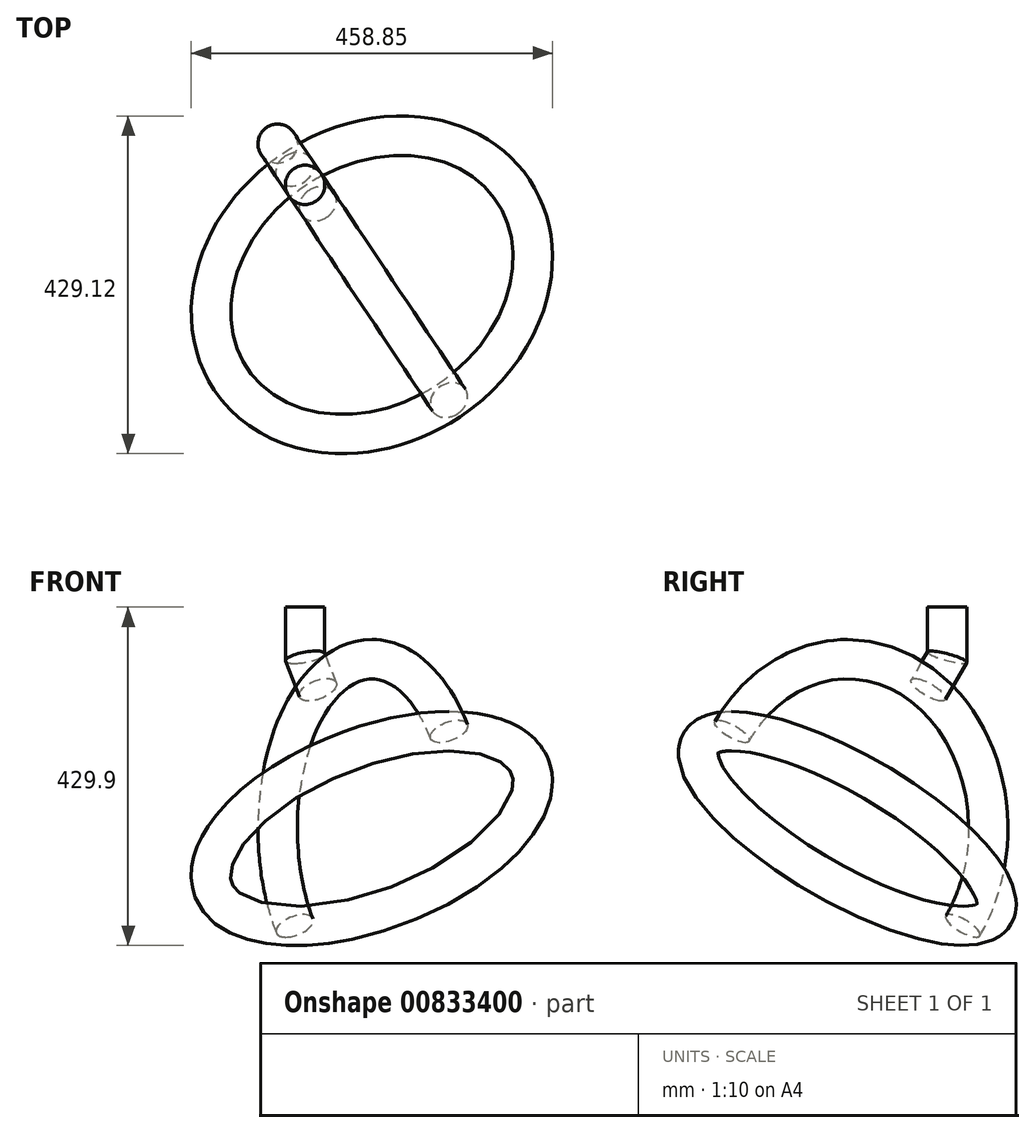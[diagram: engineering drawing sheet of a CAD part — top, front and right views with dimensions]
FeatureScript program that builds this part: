
annotation { "Feature Type Name" : "Feature", "Feature Type Description" : "" }
export const myFeature = defineFeature(function(context is Context, id is Id, definition is map)
    precondition{}
    {
        {
            var Q0;
            Q0=qCreatedBy(makeId("Front.planeOp"),FACE);
            var sketch = newSketch(context, id + "F0", { "sketchPlane" : qUnion([Q0])});
            skLineSegment(sketch, "E0", {"start": v(0, 0) * mm, "end": v(0, -63.5) * mm});
            skLineSegment(sketch, "E1", {"start": v(152.5, -281.3) * mm, "end": v(329.03, -157.7) * mm});
            skLineSegment(sketch, "E2", {"start": v(152.5, -281.3) * mm, "end": v(-24.02, -404.9) * mm});
            skArc(sketch, "E3", {"start": v(329.03, -157.7) * mm, "mid": v(28.97, -104.87) * mm, "end": v(-24.02, -404.9) * mm});
            skLineSegment(sketch, "E4", {"start": v(0, -63.5) * mm, "end": v(28.97, -104.87) * mm});
            skLineSegment(sketch, "E5", {"start": v(28.97, -104.87) * mm, "end": v(152.57, -281.4) * mm});
            skCircle(sketch, "E6", {"center": v(-24.02, -404.9) * mm, "radius": 25 * mm});
            skSolve(sketch);
        }
        {
            var Q0;
            Q0=sQuery(id+"F0.wireOp",VERTEX,"97wq7kTM-Wat1-zyJu-AWVl-G3QsEm7D3rIj.end");
            var Q1;
            Q1=sQuery(id+"F0.wireOp",EDGE,"97wq7kTM-Wat1-zyJu-AWVl-G3QsEm7D3rIj");
            var Q2;
            Q2=sQuery(id+"F0.wireOp",VERTEX,"E1.start");
            var Q3;
            Q3=sQuery(id+"F0.wireOp",EDGE,"E5");
            cPlane(context, id + "F1", {"entities" : qUnion([Q0, Q1, Q2, Q3]), "cplaneType" : CPlaneType.LINE_POINT, "offset" : 25.4 * mm, "width" : 152.4 * mm, "height" : 152.4 * mm});
        }
        {
            var Q0;
            Q0=qCreatedBy(id+"F1.planeOp",FACE);
            var sketch = newSketch(context, id + "F2", { "sketchPlane" : qUnion([Q0])});
            skCircle(sketch, "E7", {"center": v(-36.25, 0.07) * mm, "radius": 215.5 * mm});
            skCircle(sketch, "E8", {"center": v(-251.74, 0) * mm, "radius": 25 * mm});
            skSolve(sketch);
        }
        {
            var Q0;
            Q0=qCreatedBy(makeId("Top.planeOp"),FACE);
            var sketch = newSketch(context, id + "F3", { "sketchPlane" : qUnion([Q0])});
            skCircle(sketch, "E9", {"center": v(0, 0) * mm, "radius": 25 * mm});
            skSolve(sketch);
        }
        {
            var Q0;
            Q0=makeQuery(id+"F3.imprint","IMPRINT",FACE,{"disambiguationData":[TD([[makeQuery(id+"F3.imprint","IMPRINT",EDGE,{"derivedFrom":sQuery(id+"F3.wireOp",EDGE,"E9")}),1.0]])]});
            var Q1;
            Q1=sQuery(id+"F3.wireOp",EDGE,"E9");
            var Q2;
            Q2=sQuery(id+"F0.wireOp",EDGE,"E0");
            var Q3;
            Q3=sQuery(id+"F0.wireOp",EDGE,"E4");
            sweep(context, id + "F4", {"profiles" : qUnion([Q0]), "surfaceProfiles" : qUnion([Q1]), "path" : qUnion([Q2, Q3])});
        }
        {
            var Q0;
            {var subQ0=sQuery(id+"F2.wireOp",EDGE,"E8");var subQ1=sQuery(id+"F2.wireOp",EDGE,"E7");var subQ2=makeQuery(id+"F2.imprint","INTERSECT",VERTEX,{"disambiguationData":[OD(0.0)],"derivedFrom":[subQ1,subQ0]});Q0=makeQuery(id+"F2.imprint","IMPRINT",FACE,{"disambiguationData":[TD([[makeQuery(id+"F2.imprint","IMPRINT",EDGE,{"disambiguationData":[TD([[subQ2,-1.0]])],"derivedFrom":subQ1}),-1.0]])]});}
            var Q1;
            {var subQ0=sQuery(id+"F2.wireOp",EDGE,"E8");var subQ1=sQuery(id+"F2.wireOp",EDGE,"E7");var subQ2=makeQuery(id+"F2.imprint","INTERSECT",VERTEX,{"disambiguationData":[OD(0.0)],"derivedFrom":[subQ1,subQ0]});Q1=makeQuery(id+"F2.imprint","IMPRINT",FACE,{"disambiguationData":[TD([[makeQuery(id+"F2.imprint","IMPRINT",EDGE,{"disambiguationData":[TD([[subQ2,-1.0]])],"derivedFrom":subQ1}),1.0]])]});}
            var Q2;
            Q2=sQuery(id+"F0.wireOp",EDGE,"E3");
            sweep(context, id + "F5", {"profiles" : qUnion([Q0, Q1]), "path" : qUnion([Q2])});
        }
        {
            var Q0;
            {var subQ0=sQuery(id+"F0.wireOp",EDGE,"E3");var subQ1=sQuery(id+"F0.wireOp",EDGE,"E2");var subQ2=makeQuery(id+"F0.imprint","INTERSECT",VERTEX,{"derivedFrom":[subQ1,subQ0]});Q0=makeQuery(id+"F0.imprint","IMPRINT",FACE,{"disambiguationData":[TD([[makeQuery(id+"F0.imprint","IMPRINT",EDGE,{"disambiguationData":[TD([[subQ2,1.0]])],"derivedFrom":subQ1}),1.0]])]});}
            var Q1;
            {var subQ0=sQuery(id+"F0.wireOp",EDGE,"E3");var subQ1=sQuery(id+"F0.wireOp",EDGE,"E2");var subQ2=makeQuery(id+"F0.imprint","INTERSECT",VERTEX,{"derivedFrom":[subQ1,subQ0]});Q1=makeQuery(id+"F0.imprint","IMPRINT",FACE,{"disambiguationData":[TD([[makeQuery(id+"F0.imprint","IMPRINT",EDGE,{"disambiguationData":[TD([[subQ2,1.0]])],"derivedFrom":subQ1}),-1.0]])]});}
            var Q2;
            Q2=sQuery(id+"F2.wireOp",EDGE,"E7");
            sweep(context, id + "F6", {"profiles" : qUnion([Q0, Q1]), "path" : qUnion([Q2])});
        }
        {
            var Q0;
            Q0=makeQuery(id+"F5.opSweep","SWEPT_BODY",BODY,{"disambiguationData":[OSD([sQuery(id+"F0.wireOp",EDGE,"E3"),sQuery(id+"F2.wireOp",EDGE,"E8")])]});
            var Q1;
            Q1=makeQuery(id+"F6.opSweep","SWEPT_BODY",BODY,{"disambiguationData":[OSD([sQuery(id+"F0.wireOp",EDGE,"E6"),sQuery(id+"F2.wireOp",EDGE,"E7")])]});
            var Q2;
            Q2=makeQuery(id+"F4.opSweep","SWEPT_BODY",BODY,{"disambiguationData":[OSD([sQuery(id+"F0.wireOp",EDGE,"E4"),sQuery(id+"F3.wireOp",EDGE,"E9")])]});
            var Q3;
            Q3=sQuery(id+"F0.wireOp",EDGE,"E0");
            transform(context, id + "F7", {"entities" : qUnion([Q0, Q1, Q2]), "transformType" : TransformType.ROTATION, "transformAxis" : qUnion([Q3]), "angle" : 191.25 * degree, "makeCopy" : false});
        }
        {
            var Q0;
            Q0=makeQuery(id+"F5.opSweep","SWEPT_BODY",BODY,{"disambiguationData":[OSD([sQuery(id+"F0.wireOp",EDGE,"E3"),sQuery(id+"F2.wireOp",EDGE,"E8")])]});
            var Q1;
            Q1=makeQuery(id+"F6.opSweep","SWEPT_BODY",BODY,{"disambiguationData":[OSD([sQuery(id+"F0.wireOp",EDGE,"E6"),sQuery(id+"F2.wireOp",EDGE,"E7")])]});
            var Q2;
            Q2=makeQuery(id+"F4.opSweep","SWEPT_BODY",BODY,{"disambiguationData":[OSD([sQuery(id+"F0.wireOp",EDGE,"E4"),sQuery(id+"F3.wireOp",EDGE,"E9")])]});
            var Q3;
            Q3=sQuery(id+"F0.wireOp",EDGE,"E0");
            transform(context, id + "F8", {"entities" : qUnion([Q0, Q1, Q2]), "transformType" : TransformType.ROTATION, "transformAxis" : qUnion([Q3]), "angle" : 225 * degree, "makeCopy" : false});
        }
    });
